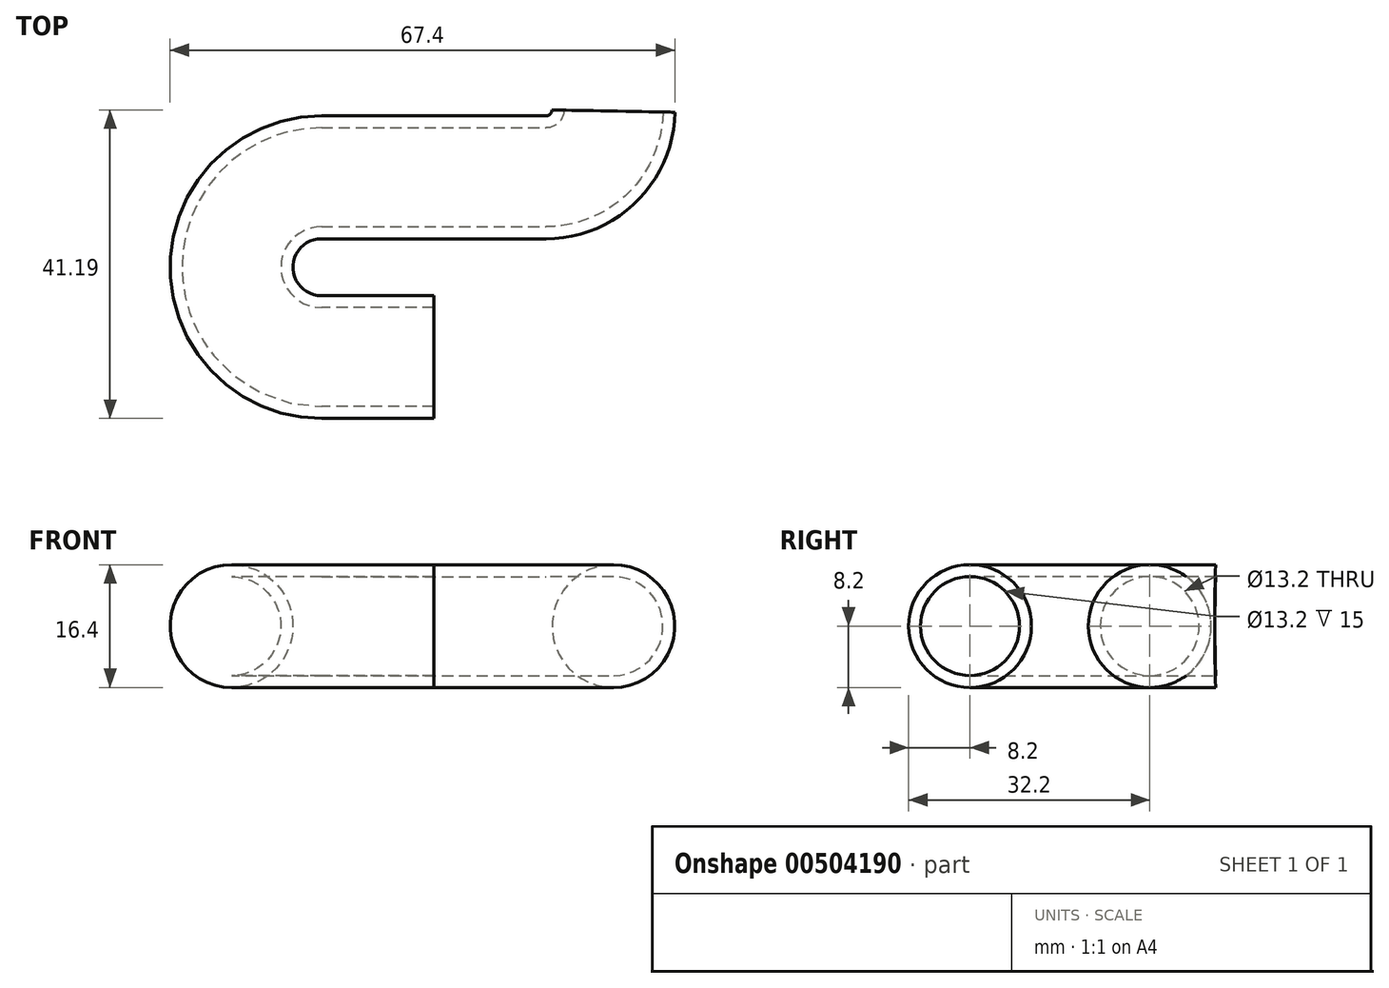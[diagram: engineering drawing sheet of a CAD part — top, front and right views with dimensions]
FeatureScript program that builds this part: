
annotation { "Feature Type Name" : "Feature", "Feature Type Description" : "" }
export const myFeature = defineFeature(function(context is Context, id is Id, definition is map)
    precondition{}
    {
        {
            var Q0;
            Q0=qCreatedBy(makeId("Top.planeOp"),FACE);
            var sketch = newSketch(context, id + "F0", { "sketchPlane" : qUnion([Q0])});
            skLineSegment(sketch, "E0", {"start": v(0, 0) * mm, "end": v(-15, 0) * mm});
            skArc(sketch, "E1", {"start": v(-15, 24) * mm, "mid": v(-27, 12) * mm, "end": v(-15, 0) * mm});
            skLineSegment(sketch, "E2", {"start": v(-15, 24) * mm, "end": v(15, 24) * mm});
            skArc(sketch, "E3", {"start": v(15, 24) * mm, "mid": v(21.3, 26.58) * mm, "end": v(24, 32.83) * mm});
            skSolve(sketch);
        }
        {
            var Q0;
            Q0=qCreatedBy(makeId("Right.planeOp"),FACE);
            var sketch = newSketch(context, id + "F1", { "sketchPlane" : qUnion([Q0])});
            skCircle(sketch, "E4", {"center": v(0, 0) * mm, "radius": 6.6 * mm});
            skCircle(sketch, "E5", {"center": v(0, 0) * mm, "radius": 8.2 * mm});
            skSolve(sketch);
        }
        {
            var Q0;
            Q0=makeQuery(id+"F1.imprint","IMPRINT",FACE,{"disambiguationData":[TD([[makeQuery(id+"F1.imprint","IMPRINT",EDGE,{"derivedFrom":sQuery(id+"F1.wireOp",EDGE,"E4")}),-1.0]])]});
            var Q1;
            Q1 = qSketchRegion(id + "F0", true);
            var Q2;
            Q2=sQuery(id+"F1.wireOp",EDGE,"E5");
            var Q3;
            Q3=sQuery(id+"F1.wireOp",EDGE,"E4");
            var Q4;
            Q4=sQuery(id+"F0.wireOp",EDGE,"E0");
            var Q5;
            Q5=sQuery(id+"F0.wireOp",EDGE,"E1");
            var Q6;
            Q6=sQuery(id+"F0.wireOp",EDGE,"E2");
            var Q7;
            Q7=sQuery(id+"F0.wireOp",EDGE,"E3");
            sweep(context, id + "F2", {"profiles" : qUnion([Q0, Q1]), "surfaceProfiles" : qUnion([Q2, Q3]), "path" : qUnion([Q4, Q5, Q6, Q7])});
        }
    });
